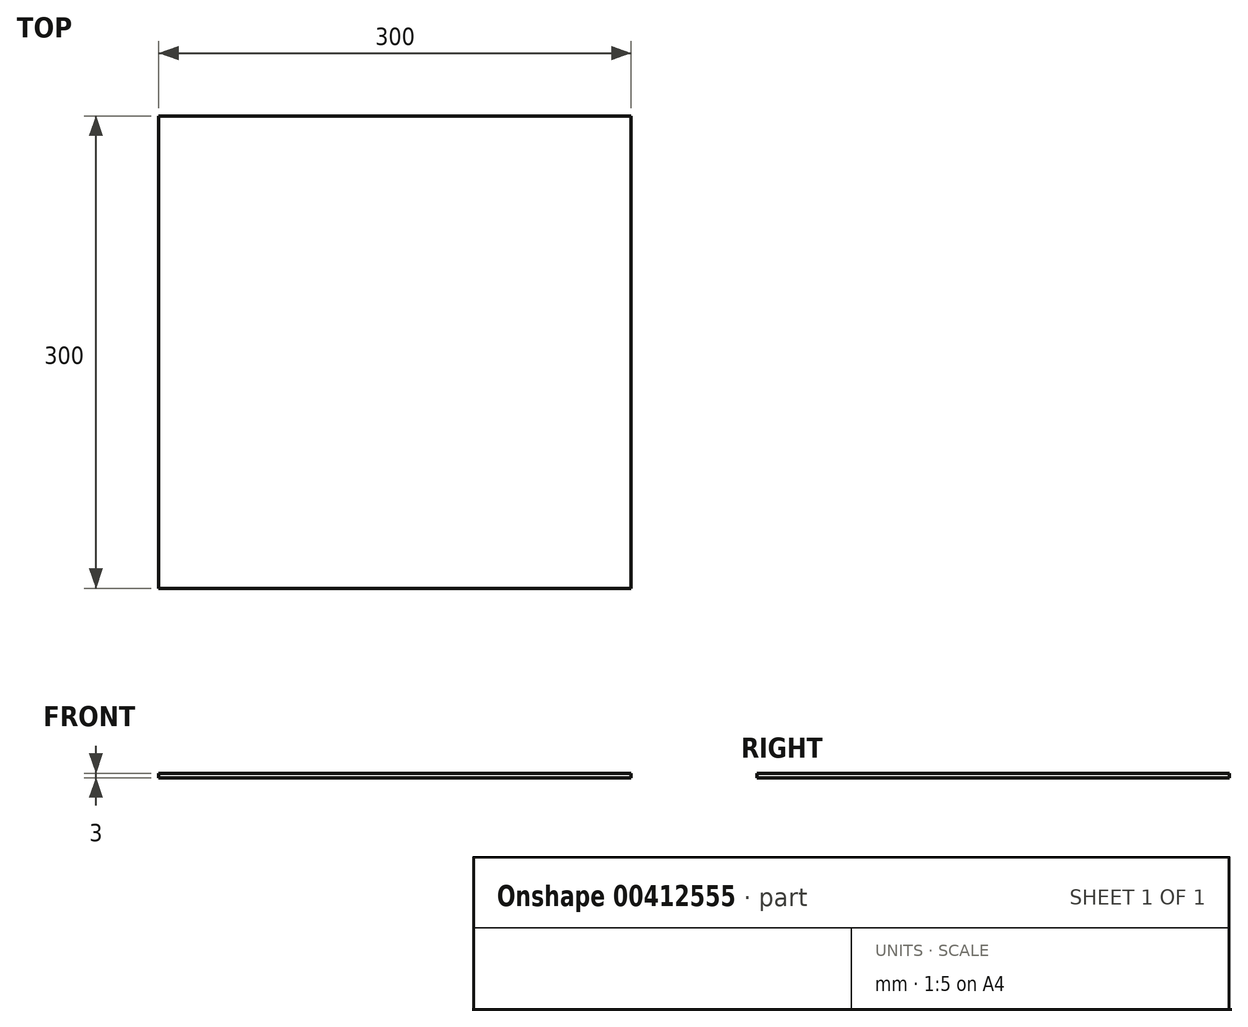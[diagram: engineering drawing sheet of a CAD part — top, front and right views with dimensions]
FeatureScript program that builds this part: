
annotation { "Feature Type Name" : "Feature", "Feature Type Description" : "" }
export const myFeature = defineFeature(function(context is Context, id is Id, definition is map)
    precondition{}
    {
        {
            var Q0;
            Q0=qCreatedBy(makeId("Top.planeOp"),FACE);
            var sketch = newSketch(context, id + "F0", { "sketchPlane" : qUnion([Q0])});
            skLineSegment(sketch, "E0.bottom", {"start": v(-146.44, 193.34) * mm, "end": v(153.56, 193.34) * mm});
            skLineSegment(sketch, "E0.top", {"start": v(-146.44, -106.66) * mm, "end": v(153.56, -106.66) * mm});
            skLineSegment(sketch, "E0.left", {"start": v(-146.44, 193.34) * mm, "end": v(-146.44, -106.66) * mm});
            skLineSegment(sketch, "E0.right", {"start": v(153.56, 193.34) * mm, "end": v(153.56, -106.66) * mm});
            skSolve(sketch);
        }
        {
            var Q0;
            Q0=makeQuery(id+"F0.imprint","IMPRINT",FACE,{"disambiguationData":[TD([[makeQuery(id+"F0.imprint","IMPRINT",EDGE,{"derivedFrom":sQuery(id+"F0.wireOp",EDGE,"E0.bottom")}),-1.0]])]});
            var sketch = newSketch(context, id + "F1", { "sketchPlane" : qUnion([Q0])});
            skLineSegment(sketch, "E1.bottom", {"start": v(-73.94, -77.66) * mm, "end": v(81.06, -77.66) * mm});
            skLineSegment(sketch, "E1.top", {"start": v(-73.94, -91.66) * mm, "end": v(81.06, -91.66) * mm});
            skLineSegment(sketch, "E1.left", {"start": v(-73.94, -77.66) * mm, "end": v(-73.94, -91.66) * mm});
            skLineSegment(sketch, "E1.right", {"start": v(81.06, -77.66) * mm, "end": v(81.06, -91.66) * mm});
            skSolve(sketch);
        }
        {
            var Q0;
            Q0=makeQuery(id+"F0.imprint","IMPRINT",FACE,{"disambiguationData":[TD([[makeQuery(id+"F0.imprint","IMPRINT",EDGE,{"derivedFrom":sQuery(id+"F0.wireOp",EDGE,"E0.bottom")}),-1.0]])]});
            extrude(context, id + "F2", {"entities" : qUnion([Q0]), "depth" : 3 * mm});
        }
    });
